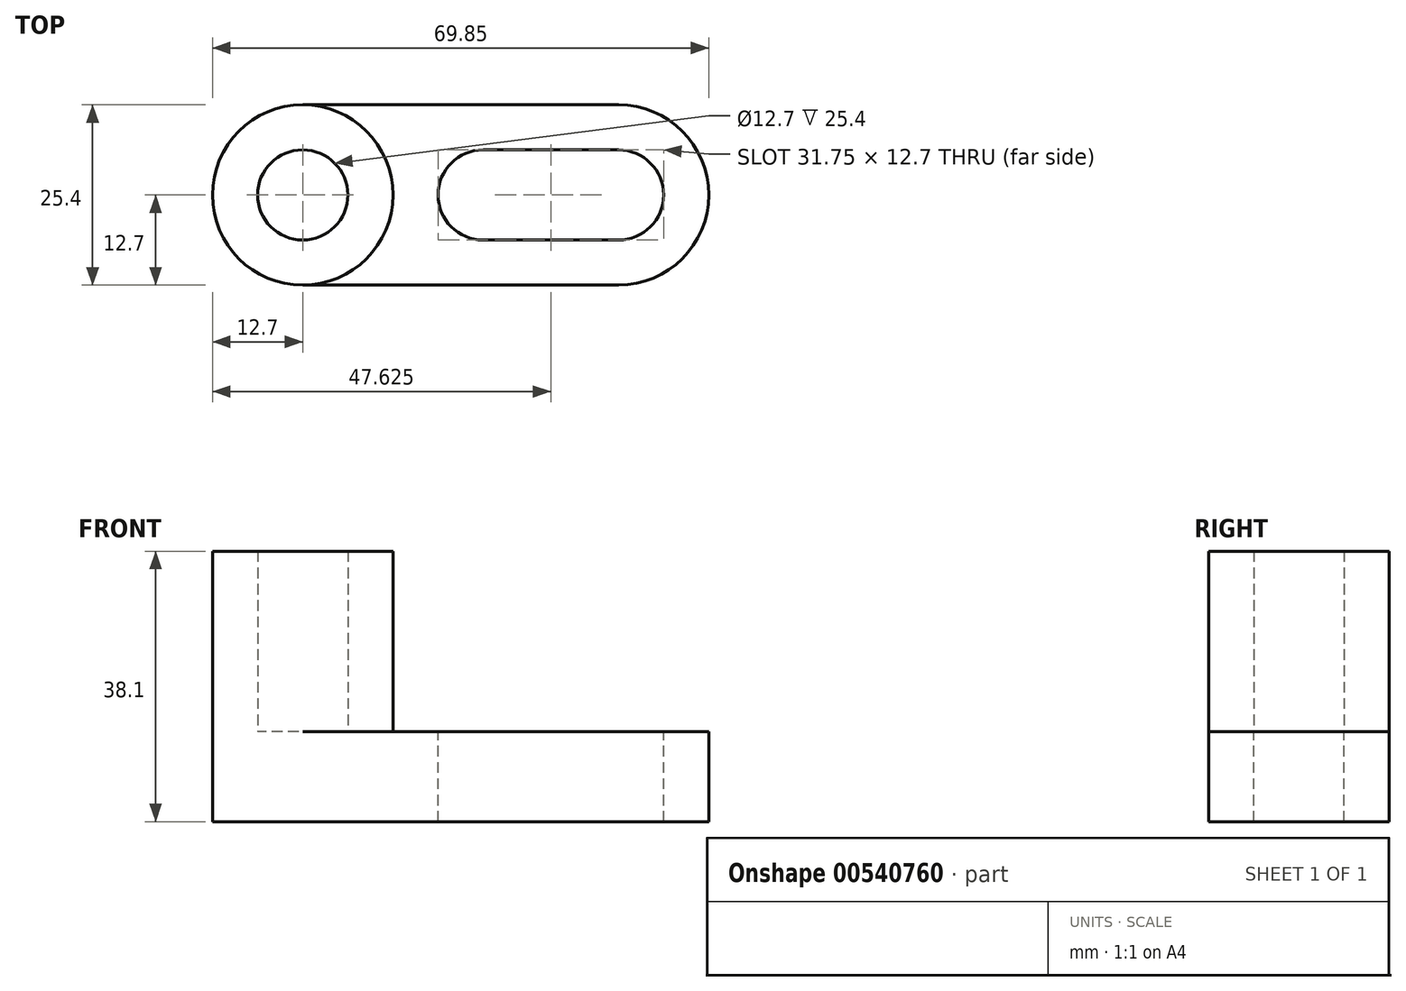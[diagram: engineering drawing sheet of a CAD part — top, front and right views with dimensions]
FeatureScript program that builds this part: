
annotation { "Feature Type Name" : "Feature", "Feature Type Description" : "" }
export const myFeature = defineFeature(function(context is Context, id is Id, definition is map)
    precondition{}
    {
        {
            var Q0;
            Q0=qCreatedBy(makeId("Front.planeOp"),FACE);
            var sketch = newSketch(context, id + "F0", { "sketchPlane" : qUnion([Q0])});
            skLineSegment(sketch, "E0", {"start": v(0, 0) * mm, "end": v(69.85, 0) * mm});
            skLineSegment(sketch, "E1", {"start": v(69.85, 0) * mm, "end": v(69.85, 12.7) * mm});
            skLineSegment(sketch, "E2", {"start": v(69.85, 12.7) * mm, "end": v(0, 12.7) * mm});
            skLineSegment(sketch, "E3", {"start": v(0, 12.7) * mm, "end": v(0, 0) * mm});
            skSolve(sketch);
        }
        {
            var Q0;
            Q0 = qSketchRegion(id + "F0", true);
            extrude(context, id + "F1", {"entities" : qUnion([Q0]), "depth" : 25.4 * mm, "offsetDistance" : 25.4 * mm});
        }
        {
            var Q0;
            Q0=makeQuery(id+"F1.opExtrude","SWEPT_FACE",FACE,{"disambiguationData":[OSD([sQuery(id+"F0.wireOp",EDGE,"E2")])]});
            var sketch = newSketch(context, id + "F2", { "sketchPlane" : qUnion([Q0])});
            skCircle(sketch, "E4", {"center": v(12.7, -12.7) * mm, "radius": 6.35 * mm});
            skCircle(sketch, "E5", {"center": v(12.7, -12.7) * mm, "radius": 12.7 * mm});
            skSolve(sketch);
        }
        {
            var Q0;
            Q0 = qSketchRegion(id + "F2", true);
            extrude(context, id + "F3", {"entities" : qUnion([Q0]), "operationType" : NewBodyOperationType.ADD, "depth" : 25.4 * mm, "offsetDistance" : 25.4 * mm});
        }
        {
            var Q0;
            {var subQ0=sQuery(id+"F0.wireOp",EDGE,"E3");var subQ1=sQuery(id+"F0.wireOp",EDGE,"E2");var subQ2=makeQuery(id+"F1.opExtrude","SWEPT_FACE",FACE,{"disambiguationData":[OSD([subQ1])]});Q0=makeQuery(id+"F3.boolean.opBoolean","SPLIT",FACE,{"disambiguationData":[TD([makeQuery(id+"F1.opExtrude","CAP_FACE",FACE,{"disambiguationData":[OSD([sQuery(id+"F0.wireOp",EDGE,"E0"),sQuery(id+"F0.wireOp",EDGE,"E1"),subQ1,subQ0])],"isStart":false}),subQ2,makeQuery(id+"F1.opExtrude","SWEPT_FACE",FACE,{"disambiguationData":[OSD([subQ0])]}),makeQuery(id+"F3.opExtrude","SWEPT_FACE",FACE,{"disambiguationData":[OSD([sQuery(id+"F2.wireOp",EDGE,"E5")])]})])],"derivedFrom":subQ2});}
            var Q1;
            {var subQ0=sQuery(id+"F0.wireOp",EDGE,"E3");var subQ1=sQuery(id+"F0.wireOp",EDGE,"E2");var subQ2=makeQuery(id+"F1.opExtrude","SWEPT_FACE",FACE,{"disambiguationData":[OSD([subQ1])]});Q1=makeQuery(id+"F3.boolean.opBoolean","SPLIT",FACE,{"disambiguationData":[TD([makeQuery(id+"F1.opExtrude","CAP_FACE",FACE,{"disambiguationData":[OSD([sQuery(id+"F0.wireOp",EDGE,"E0"),sQuery(id+"F0.wireOp",EDGE,"E1"),subQ1,subQ0])],"isStart":true}),subQ2,makeQuery(id+"F1.opExtrude","SWEPT_FACE",FACE,{"disambiguationData":[OSD([subQ0])]}),makeQuery(id+"F3.opExtrude","SWEPT_FACE",FACE,{"disambiguationData":[OSD([sQuery(id+"F2.wireOp",EDGE,"E5")])]})])],"derivedFrom":subQ2});}
            extrude(context, id + "F4", {"entities" : qUnion([Q0, Q1]), "operationType" : NewBodyOperationType.REMOVE, "oppositeDirection" : true, "depth" : 25.4 * mm, "offsetDistance" : 25.4 * mm});
        }
        {
            var Q0;
            {var subQ0=sQuery(id+"F0.wireOp",EDGE,"E2");var subQ1=makeQuery(id+"F1.opExtrude","SWEPT_FACE",FACE,{"disambiguationData":[OSD([subQ0])]});var subQ2=sQuery(id+"F0.wireOp",EDGE,"E1");var subQ3=sQuery(id+"F0.wireOp",EDGE,"E3");var subQ4=sQuery(id+"F0.wireOp",EDGE,"E0");Q0=makeQuery(id+"F3.boolean.opBoolean","SPLIT",FACE,{"disambiguationData":[TD([makeQuery(id+"F1.opExtrude","CAP_FACE",FACE,{"disambiguationData":[OSD([subQ4,subQ2,subQ0,subQ3])],"isStart":true}),makeQuery(id+"F1.opExtrude","CAP_FACE",FACE,{"disambiguationData":[OSD([subQ4,subQ2,subQ0,subQ3])],"isStart":false}),makeQuery(id+"F1.opExtrude","SWEPT_FACE",FACE,{"disambiguationData":[OSD([subQ2])]}),subQ1,makeQuery(id+"F3.opExtrude","SWEPT_FACE",FACE,{"disambiguationData":[OSD([sQuery(id+"F2.wireOp",EDGE,"E5")])]})])],"derivedFrom":subQ1});}
            var sketch = newSketch(context, id + "F5", { "sketchPlane" : qUnion([Q0])});
            skCircle(sketch, "E6", {"center": v(38.1, -12.7) * mm, "radius": 6.35 * mm});
            skCircle(sketch, "E7", {"center": v(57.15, -12.7) * mm, "radius": 6.35 * mm});
            skLineSegment(sketch, "E8", {"start": v(38.1, -6.35) * mm, "end": v(57.15, -6.35) * mm});
            skLineSegment(sketch, "E9", {"start": v(57.15, -19.05) * mm, "end": v(38.1, -19.05) * mm});
            skArc(sketch, "E10", {"start": v(57.15, -25.4) * mm, "mid": v(69.85, -12.7) * mm, "end": v(57.15, 0) * mm});
            skSolve(sketch);
        }
        {
            var Q0;
            {var subQ0=sQuery(id+"F5.wireOp",EDGE,"E6");var subQ1=makeQuery(id+"F5.imprint","INTERSECT",VERTEX,{"derivedFrom":[subQ0,sQuery(id+"F5.wireOp",EDGE,"E8")]});Q0=makeQuery(id+"F5.imprint","IMPRINT",FACE,{"disambiguationData":[TD([[makeQuery(id+"F5.imprint","IMPRINT",EDGE,{"disambiguationData":[TD([[subQ1,-1.0]])],"derivedFrom":subQ0}),1.0]])]});}
            var Q1;
            {var subQ0=sQuery(id+"F5.wireOp",EDGE,"E8");Q1=makeQuery(id+"F5.imprint","IMPRINT",FACE,{"disambiguationData":[TD([[makeQuery(id+"F5.imprint","IMPRINT",EDGE,{"derivedFrom":subQ0}),-1.0]])]});}
            var Q2;
            {var subQ0=sQuery(id+"F5.wireOp",EDGE,"E7");var subQ1=makeQuery(id+"F5.imprint","INTERSECT",VERTEX,{"derivedFrom":[subQ0,sQuery(id+"F5.wireOp",EDGE,"E8")]});Q2=makeQuery(id+"F5.imprint","IMPRINT",FACE,{"disambiguationData":[TD([[makeQuery(id+"F5.imprint","IMPRINT",EDGE,{"disambiguationData":[TD([[subQ1,-1.0]])],"derivedFrom":subQ0}),1.0]])]});}
            var Q3;
            {var subQ0=sQuery(id+"F5.wireOp",EDGE,"E10");var subQ1=sQuery(id+"F0.wireOp",EDGE,"E2");var subQ2=sQuery(id+"F0.wireOp",EDGE,"E1");var subQ5=makeQuery(id+"F1.opExtrude","SWEPT_EDGE",EDGE,{"disambiguationData":[OSD([subQ2,subQ1])]});var subQ6=makeQuery(id+"F5.imprint","INTERSECT",VERTEX,{"derivedFrom":[subQ5,subQ0]});Q3=makeQuery(id+"F5.imprint","IMPRINT",FACE,{"disambiguationData":[TD([[makeQuery(id+"F5.imprint","IMPRINT",EDGE,{"disambiguationData":[TD([[subQ6,-1.0]])],"derivedFrom":subQ0}),-1.0]])]});}
            var Q4;
            {var subQ0=sQuery(id+"F5.wireOp",EDGE,"E10");var subQ1=sQuery(id+"F0.wireOp",EDGE,"E2");var subQ2=sQuery(id+"F0.wireOp",EDGE,"E1");var subQ5=makeQuery(id+"F1.opExtrude","SWEPT_EDGE",EDGE,{"disambiguationData":[OSD([subQ2,subQ1])]});var subQ6=makeQuery(id+"F5.imprint","INTERSECT",VERTEX,{"derivedFrom":[subQ5,subQ0]});Q4=makeQuery(id+"F5.imprint","IMPRINT",FACE,{"disambiguationData":[TD([[makeQuery(id+"F5.imprint","IMPRINT",EDGE,{"disambiguationData":[TD([[subQ6,1.0]])],"derivedFrom":subQ0}),-1.0]])]});}
            extrude(context, id + "F6", {"entities" : qUnion([Q0, Q1, Q2, Q3, Q4]), "operationType" : NewBodyOperationType.REMOVE, "oppositeDirection" : true, "depth" : 25.4 * mm, "offsetDistance" : 25.4 * mm});
        }
    });
